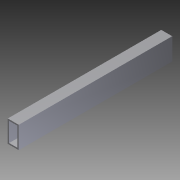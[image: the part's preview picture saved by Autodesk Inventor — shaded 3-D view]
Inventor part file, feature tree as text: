
AUTODESK INVENTOR PART (.ipt)
format: ipt  version: 2012 (Build 160160000, 160)  size: 75,264 bytes
history: native  units: in
note: dims shown in document units (in); Inventor stores cm internally (conversion verified against a paired STEP export)
features: extrude x1, sketch x1
ambient origin geometry x8: Origin, YZ Plane, XZ Plane, XY Plane, X Axis, Y Axis, Z Axis, Center Point
bodies: Solid1 (feature_tree)
feature tree (2):
  extrude  "Extrusion1"  Depth=1.0in
  sketch  "Sketch1"  dims[d0=2.0in d1=1.0in d2=0.125in d3=0.125in d4=0.125in d5=0.125in d6=14.0in d7=0.0in]
